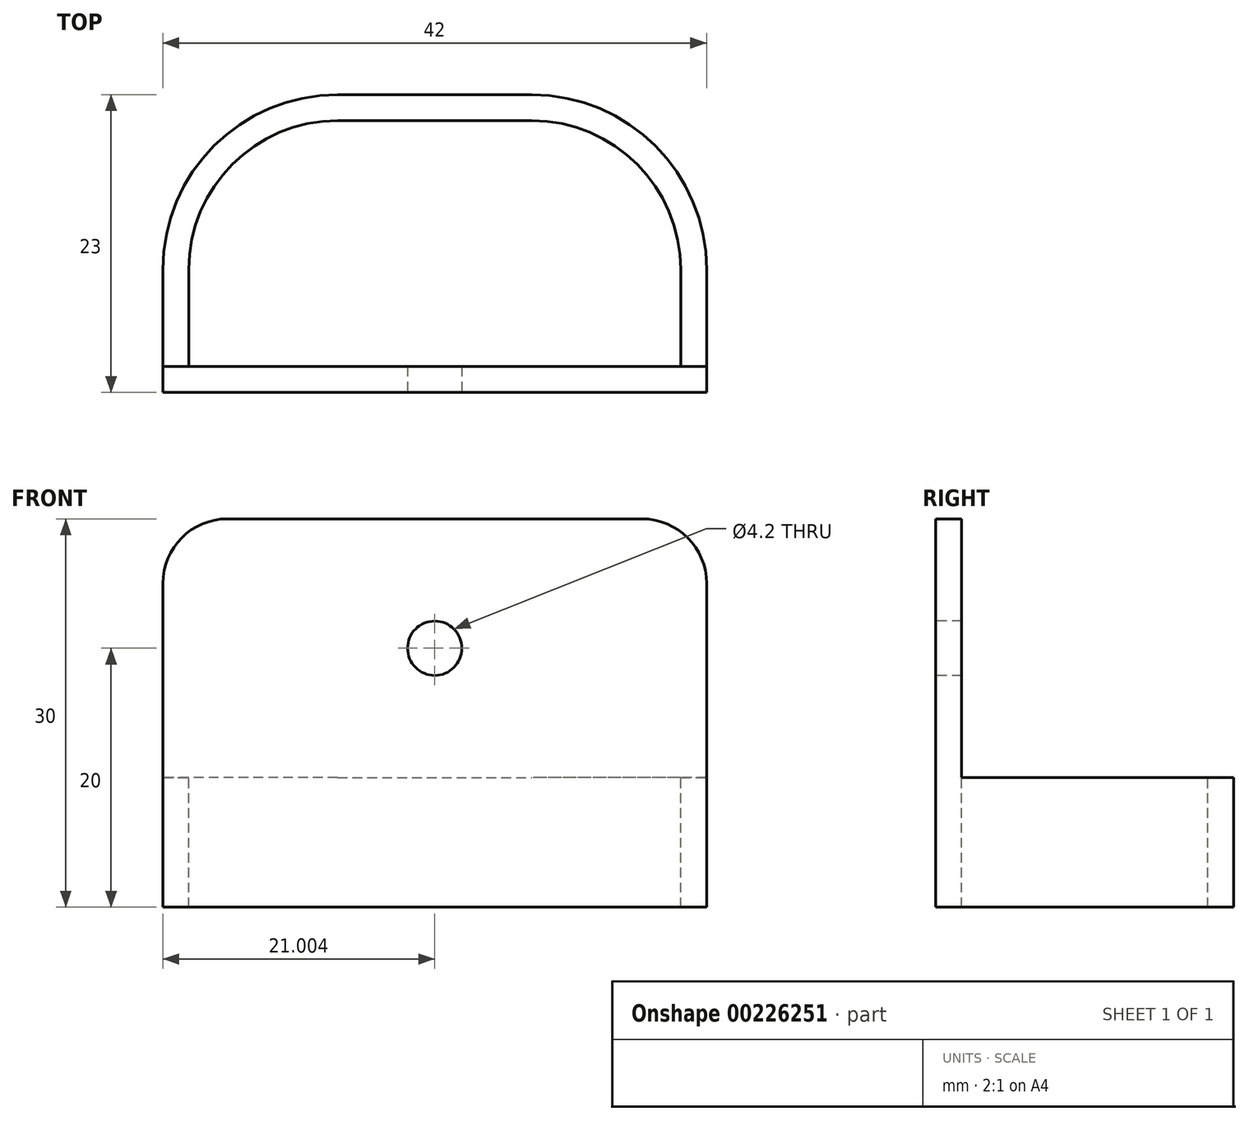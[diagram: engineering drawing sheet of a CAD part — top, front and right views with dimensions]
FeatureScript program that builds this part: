
annotation { "Feature Type Name" : "Feature", "Feature Type Description" : "" }
export const myFeature = defineFeature(function(context is Context, id is Id, definition is map)
    precondition{}
    {
        {
            var Q0;
            Q0=qCreatedBy(makeId("Top.planeOp"),FACE);
            var sketch = newSketch(context, id + "F0", { "sketchPlane" : qUnion([Q0])});
            skLineSegment(sketch, "E0.bottom", {"start": v(36.72, -41.29) * mm, "end": v(51.72, -41.29) * mm});
            skLineSegment(sketch, "E0.top", {"start": v(23.22, -64.29) * mm, "end": v(65.22, -64.29) * mm});
            skLineSegment(sketch, "E0.left", {"start": v(23.22, -54.79) * mm, "end": v(23.22, -64.29) * mm});
            skLineSegment(sketch, "E0.right", {"start": v(65.22, -54.79) * mm, "end": v(65.22, -64.29) * mm});
            skArc(sketch, "E1.filletArc", {"start": v(36.72, -41.29) * mm, "mid": v(27.18, -45.24) * mm, "end": v(23.22, -54.79) * mm});
            skArc(sketch, "E2.filletArc", {"start": v(65.22, -54.79) * mm, "mid": v(61.27, -45.24) * mm, "end": v(51.72, -41.29) * mm});
            skSolve(sketch);
        }
        {
            var Q0;
            Q0=makeQuery(id+"F0.imprint","IMPRINT",FACE,{"disambiguationData":[TD([[makeQuery(id+"F0.imprint","IMPRINT",EDGE,{"derivedFrom":sQuery(id+"F0.wireOp",EDGE,"E0.bottom")}),-1.0]])]});
            extrude(context, id + "F1", {"entities" : qUnion([Q0]), "depth" : 10 * mm});
        }
        {
            var Q0;
            Q0=makeQuery(id+"F1.opExtrude","CAP_FACE",FACE,{"disambiguationData":[OSD([sQuery(id+"F0.wireOp",EDGE,"E0.bottom"),sQuery(id+"F0.wireOp",EDGE,"E0.top"),sQuery(id+"F0.wireOp",EDGE,"E0.left"),sQuery(id+"F0.wireOp",EDGE,"E0.right"),sQuery(id+"F0.wireOp",EDGE,"E1.filletArc"),sQuery(id+"F0.wireOp",EDGE,"E2.filletArc")])],"isStart":false});
            var sketch = newSketch(context, id + "F2", { "sketchPlane" : qUnion([Q0])});
            skLineSegment(sketch, "E3.bottom", {"start": v(36.72, -43.29) * mm, "end": v(51.72, -43.29) * mm});
            skLineSegment(sketch, "E3.top", {"start": v(25.22, -62.29) * mm, "end": v(63.22, -62.29) * mm});
            skLineSegment(sketch, "E3.left", {"start": v(25.22, -54.79) * mm, "end": v(25.22, -62.29) * mm});
            skLineSegment(sketch, "E3.right", {"start": v(63.22, -54.79) * mm, "end": v(63.22, -62.29) * mm});
            skPoint(sketch, "E4.visualSharp", {"position": v(63.22, -43.29) * mm});
            skArc(sketch, "E4.filletArc", {"start": v(63.22, -54.79) * mm, "mid": v(59.86, -46.66) * mm, "end": v(51.72, -43.29) * mm});
            skPoint(sketch, "E5.visualSharp", {"position": v(25.22, -43.29) * mm});
            skArc(sketch, "E5.filletArc", {"start": v(36.72, -43.29) * mm, "mid": v(28.6, -46.66) * mm, "end": v(25.22, -54.79) * mm});
            skSolve(sketch);
        }
        {
            var Q0;
            Q0 = qSketchRegion(id + "F2", true);
            extrude(context, id + "F3", {"entities" : qUnion([Q0]), "operationType" : NewBodyOperationType.REMOVE, "oppositeDirection" : true, "depth" : 25 * mm});
        }
        {
            var Q0;
            Q0=makeQuery(id+"F1.opExtrude","CAP_FACE",FACE,{"disambiguationData":[OSD([sQuery(id+"F0.wireOp",EDGE,"E0.bottom"),sQuery(id+"F0.wireOp",EDGE,"E0.top"),sQuery(id+"F0.wireOp",EDGE,"E0.left"),sQuery(id+"F0.wireOp",EDGE,"E0.right"),sQuery(id+"F0.wireOp",EDGE,"E1.filletArc"),sQuery(id+"F0.wireOp",EDGE,"E2.filletArc")])],"isStart":false});
            var sketch = newSketch(context, id + "F4", { "sketchPlane" : qUnion([Q0])});
            skLineSegment(sketch, "E6.bottom", {"start": v(23.22, -64.29) * mm, "end": v(65.22, -64.29) * mm});
            skLineSegment(sketch, "E6.top", {"start": v(23.22, -62.29) * mm, "end": v(65.22, -62.29) * mm});
            skLineSegment(sketch, "E6.left", {"start": v(23.22, -64.29) * mm, "end": v(23.22, -62.29) * mm});
            skLineSegment(sketch, "E6.right", {"start": v(65.22, -64.29) * mm, "end": v(65.22, -62.29) * mm});
            skSolve(sketch);
        }
        {
            var Q0;
            Q0 = qSketchRegion(id + "F4", true);
            extrude(context, id + "F5", {"entities" : qUnion([Q0]), "operationType" : NewBodyOperationType.ADD, "depth" : 20 * mm});
        }
        {
            var Q0;
            Q0=makeQuery(id+"F5.boolean.opBoolean","MERGE",FACE,{"derivedFrom":[makeQuery(id+"F1.opExtrude","SWEPT_FACE",FACE,{"disambiguationData":[OSD([sQuery(id+"F0.wireOp",EDGE,"E0.top")])]}),makeQuery(id+"F5.opExtrude","SWEPT_FACE",FACE,{"disambiguationData":[OSD([sQuery(id+"F4.wireOp",EDGE,"E6.bottom")])]})]});
            var sketch = newSketch(context, id + "F6", { "sketchPlane" : qUnion([Q0])});
            skCircle(sketch, "E7", {"center": v(44.22, 20) * mm, "radius": 2.1 * mm});
            skSolve(sketch);
        }
        {
            var Q0;
            Q0 = qSketchRegion(id + "F6", true);
            extrude(context, id + "F7", {"entities" : qUnion([Q0]), "operationType" : NewBodyOperationType.REMOVE, "oppositeDirection" : true, "depth" : 4 * mm});
        }
        {
            var Q0;
            Q0=makeQuery(id+"F5.opExtrude","CAP_EDGE",EDGE,{"disambiguationData":[OSD([sQuery(id+"F4.wireOp",EDGE,"E6.right")])],"isStart":false});
            fillet(context, id + "F8", {"entities" : qUnion([Q0]), "radius" : 5 * mm, "tangentPropagation" : true, "allowEdgeOverflow" : false});
        }
        {
            var Q0;
            Q0=makeQuery(id+"F5.opExtrude","CAP_EDGE",EDGE,{"disambiguationData":[OSD([sQuery(id+"F4.wireOp",EDGE,"E6.left")])],"isStart":false});
            fillet(context, id + "F9", {"entities" : qUnion([Q0]), "radius" : 5 * mm, "tangentPropagation" : true, "allowEdgeOverflow" : false});
        }
    });
